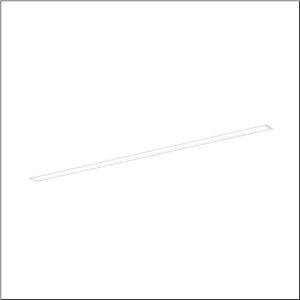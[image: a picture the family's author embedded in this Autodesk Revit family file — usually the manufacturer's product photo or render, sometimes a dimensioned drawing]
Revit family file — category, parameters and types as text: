
# Revit family: silica_21_51mx13db45wb
name_source: partatom
category: Lighting Fixtures
units: mm (PartAtom-declared; Revit-internal decimal feet)

## family parameters
Cut with Voids When Loaded = No
Host = Face
Light Source = No
Part Type = Normal
Room Calculation Point = No
Round Connector Dimension = Use Diameter
Shared = No

## types (1)
- --- (1 x LED, 4100 lm, 28.1 W, 4000K)
    Apparent Load = 28 VA
    CIE Flux Codes = 78 96 99 100 100
    Color Rendering = 80
    Color Temperature = 4000K
    Default Elevation = 1800 mm
    Description = Silica 21, office luminaire, primary optical cover: prismatic diffuser, of PMMA, CAT 2 (L<= 3000cd/m²), light emission: direct distribution, primary light characteristic: symmetric, installation type: recessed, LED, rated luminous flux: 4.100lm, luminous efficacy: 146lm/W, light colour: 840, colour temperature: 4000K, control gear: DALI 2, with terminal, 3+2-pole, max. 2.5mm², mains connection: 220..240V, AC, 50/60Hz, rated input power: 28.1W, luminaire housing, of aluminium, traffic white (RAL 9016), length: 1.528mm, width: 79mm, height: 53mm, protection rating (complete): IP20, insulation class (complete): insulation class I (protective earthing), certification: CE, ENEC, VDE, permissible operating ambient temperature: 0..+35°C, standard: EN 50419, packaging unit: 1 piece
    Height = 0 mm  [stored 0 ft]
    Lamp = 1 x LED
    Lamp Light Flux = 4100 lm
    Lamp Power = 28.1 W
    Lamp count = 1
    Length = 1527 mm
    Luminous efficacy = 146 lm/W
    Manufacturer = Siteco
    ModVariant = No
    Model = 51MX13DB45WB
    Mounting Place = Ceiling
    Mounting Type = Recessed
    Number of Poles = 1
    OnlyDefault = Yes
    Power Factor = 1
    Product Name = Silica 21
    Product group = office luminaire | ceiling recessed
    ProductGroupID = 400
    Protection Class = Protection class I
    Protection Degree = IP 20
    RLX_Detail_Level = 1
    RLX_Emergency_Light_Flux = 0 lm
    RLX_Emergency_Type = 0
    RLX_Emergency_Type_DB = No
    RlxData = <blob elided: 14293 chars, md5=df33ee04>
    Socket = socket
    Standby Power = 0 W
    System Light Flux = 4100 lm
    System Power = 28 W
    Type Comments = factory setting: luminous flux: 100 % | dim-lin: 254 | 323 mA
    Type Image = l_1251692.jpg
    URL = http://relux.com
    VarID = @adj_120809
    Voltage = 0 V
    Weight = 0.00 kg
    Width = 79 mm

note: [stored X ft] marks values corroborated as IEEE doubles in the binary element streams (Revit-internal decimal feet)

## geometry (parser evidence)
native form markers: Sweep x10
no freeform markers — native parametric forms only
